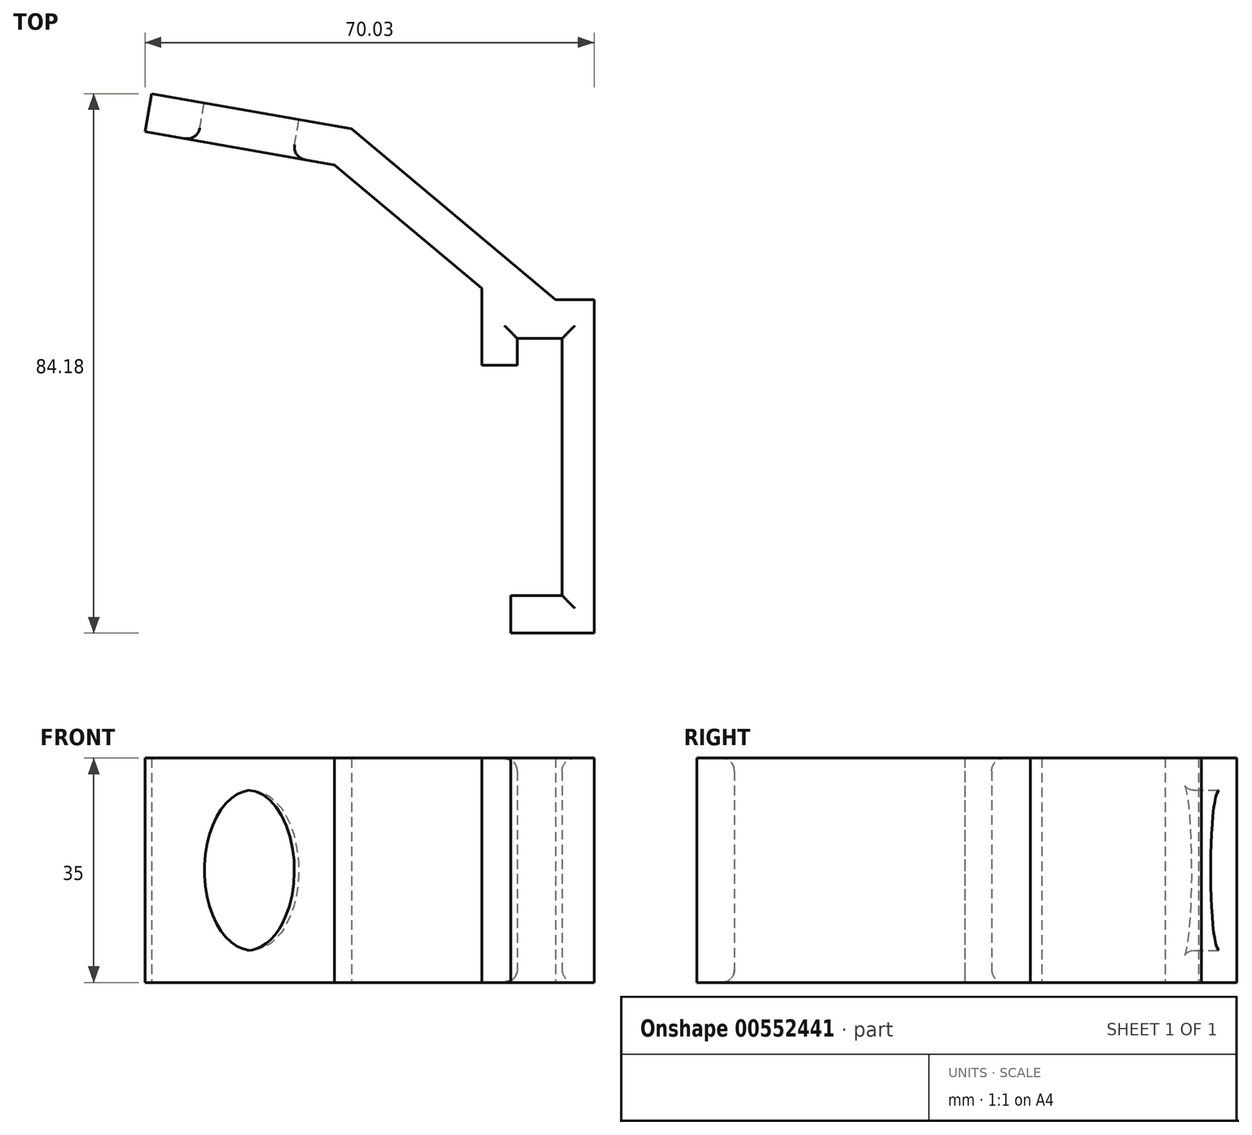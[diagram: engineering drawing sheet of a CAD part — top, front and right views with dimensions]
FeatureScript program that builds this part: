
annotation { "Feature Type Name" : "Feature", "Feature Type Description" : "" }
export const myFeature = defineFeature(function(context is Context, id is Id, definition is map)
    precondition{}
    {
        {
            var Q0;
            Q0=qCreatedBy(makeId("Top.planeOp"),FACE);
            var sketch = newSketch(context, id + "F0", { "sketchPlane" : qUnion([Q0])});
            skLineSegment(sketch, "E0", {"start": v(0, 5.88) * mm, "end": v(0, 0) * mm});
            skLineSegment(sketch, "E1", {"start": v(0, 0) * mm, "end": v(13, 0) * mm});
            skLineSegment(sketch, "E2", {"start": v(13, 0) * mm, "end": v(13, 52) * mm});
            skLineSegment(sketch, "E3", {"start": v(-4.5, 53.78) * mm, "end": v(-4.5, 41.78) * mm});
            skLineSegment(sketch, "E4", {"start": v(-4.5, 41.78) * mm, "end": v(1, 41.78) * mm});
            skLineSegment(sketch, "E5", {"start": v(1, 41.78) * mm, "end": v(1, 45.98) * mm});
            skLineSegment(sketch, "E6", {"start": v(1, 45.98) * mm, "end": v(8, 45.98) * mm});
            skLineSegment(sketch, "E7", {"start": v(8, 45.98) * mm, "end": v(8, 5.88) * mm});
            skLineSegment(sketch, "E8", {"start": v(8, 5.88) * mm, "end": v(0, 5.88) * mm});
            skLineSegment(sketch, "E9", {"start": v(-4.5, 53.78) * mm, "end": v(-27.48, 73.07) * mm});
            skLineSegment(sketch, "E10", {"start": v(6.96, 52) * mm, "end": v(-24.86, 78.7) * mm});
            skLineSegment(sketch, "E11", {"start": v(13, 52) * mm, "end": v(6.96, 52) * mm});
            skLineSegment(sketch, "E12", {"start": v(-27.48, 73.07) * mm, "end": v(-57.03, 78.27) * mm});
            skLineSegment(sketch, "E13", {"start": v(-24.86, 78.7) * mm, "end": v(-55.98, 84.18) * mm});
            skLineSegment(sketch, "E14", {"start": v(-57.03, 78.27) * mm, "end": v(-55.98, 84.18) * mm});
            skSolve(sketch);
        }
        {
            var Q0;
            Q0 = qSketchRegion(id + "F0", true);
            extrude(context, id + "F1", {"entities" : qUnion([Q0]), "depth" : 35 * mm, "offsetDistance" : 25 * mm});
        }
        {
            var Q0;
            Q0=makeQuery(id+"F1.opExtrude","SWEPT_FACE",FACE,{"disambiguationData":[OSD([sQuery(id+"F0.wireOp",EDGE,"E13")])]});
            var sketch = newSketch(context, id + "F2", { "sketchPlane" : qUnion([Q0])});
            skEllipse(sketch, "E15", {"center": v(53.95, 17.5) * mm, "majorRadius": 12.5 * mm, "minorRadius": 7.5 * mm, "majorAxis": v(0, 1)});
            skPoint(sketch, "E15.centerSnap0", {"position": v(53.95, 35) * mm});
            skPoint(sketch, "E15.centerSnap1", {"position": v(69.75, 17.5) * mm});
            skSolve(sketch);
        }
        {
            var Q0;
            Q0 = qSketchRegion(id + "F2", true);
            extrude(context, id + "F3", {"entities" : qUnion([Q0]), "operationType" : NewBodyOperationType.REMOVE, "oppositeDirection" : true, "depth" : 25 * mm, "offsetDistance" : 25 * mm});
        }
        {
            var Q0;
            Q0=makeQuery(id+"F1.opExtrude","CAP_EDGE",EDGE,{"disambiguationData":[OSD([sQuery(id+"F0.wireOp",EDGE,"E6")])],"isStart":false});
            var Q1;
            Q1=makeQuery(id+"F1.opExtrude","CAP_EDGE",EDGE,{"disambiguationData":[OSD([sQuery(id+"F0.wireOp",EDGE,"E7")])],"isStart":false});
            var Q2;
            Q2=makeQuery(id+"F1.opExtrude","CAP_EDGE",EDGE,{"disambiguationData":[OSD([sQuery(id+"F0.wireOp",EDGE,"E8")])],"isStart":false});
            var Q3;
            Q3=makeQuery(id+"F1.opExtrude","CAP_EDGE",EDGE,{"disambiguationData":[OSD([sQuery(id+"F0.wireOp",EDGE,"E5")])],"isStart":false});
            var Q4;
            Q4=makeQuery(id+"F1.opExtrude","CAP_EDGE",EDGE,{"disambiguationData":[OSD([sQuery(id+"F0.wireOp",EDGE,"E8")])],"isStart":true});
            var Q5;
            Q5=makeQuery(id+"F1.opExtrude","CAP_EDGE",EDGE,{"disambiguationData":[OSD([sQuery(id+"F0.wireOp",EDGE,"E7")])],"isStart":true});
            var Q6;
            Q6=makeQuery(id+"F1.opExtrude","CAP_EDGE",EDGE,{"disambiguationData":[OSD([sQuery(id+"F0.wireOp",EDGE,"E6")])],"isStart":true});
            var Q7;
            Q7=makeQuery(id+"F1.opExtrude","CAP_EDGE",EDGE,{"disambiguationData":[OSD([sQuery(id+"F0.wireOp",EDGE,"E5")])],"isStart":true});
            fillet(context, id + "F4", {"entities" : qUnion([Q0, Q1, Q2, Q3, Q4, Q5, Q6, Q7]), "radius" : 2 * mm, "tangentPropagation" : true, "allowEdgeOverflow" : false});
        }
        {
            var Q0;
            Q0=makeQuery(id+"F3.boolean.opBoolean","COPY",EDGE,{"derivedFrom":makeQuery(id+"F3.opExtrude","CAP_EDGE",EDGE,{"disambiguationData":[OSD([sQuery(id+"F2.wireOp",EDGE,"E15")])],"isStart":true})});
            var Q1;
            Q1=makeQuery(id+"F3.boolean.opBoolean","INTERSECT",EDGE,{"derivedFrom":[makeQuery(id+"F1.opExtrude","SWEPT_FACE",FACE,{"disambiguationData":[OSD([sQuery(id+"F0.wireOp",EDGE,"E12")])]}),makeQuery(id+"F3.opExtrude","SWEPT_FACE",FACE,{"disambiguationData":[OSD([sQuery(id+"F2.wireOp",EDGE,"E15")])]})]});
            fillet(context, id + "F5", {"entities" : qUnion([Q0, Q1]), "radius" : 2 * mm, "tangentPropagation" : true, "allowEdgeOverflow" : false});
        }
    });
